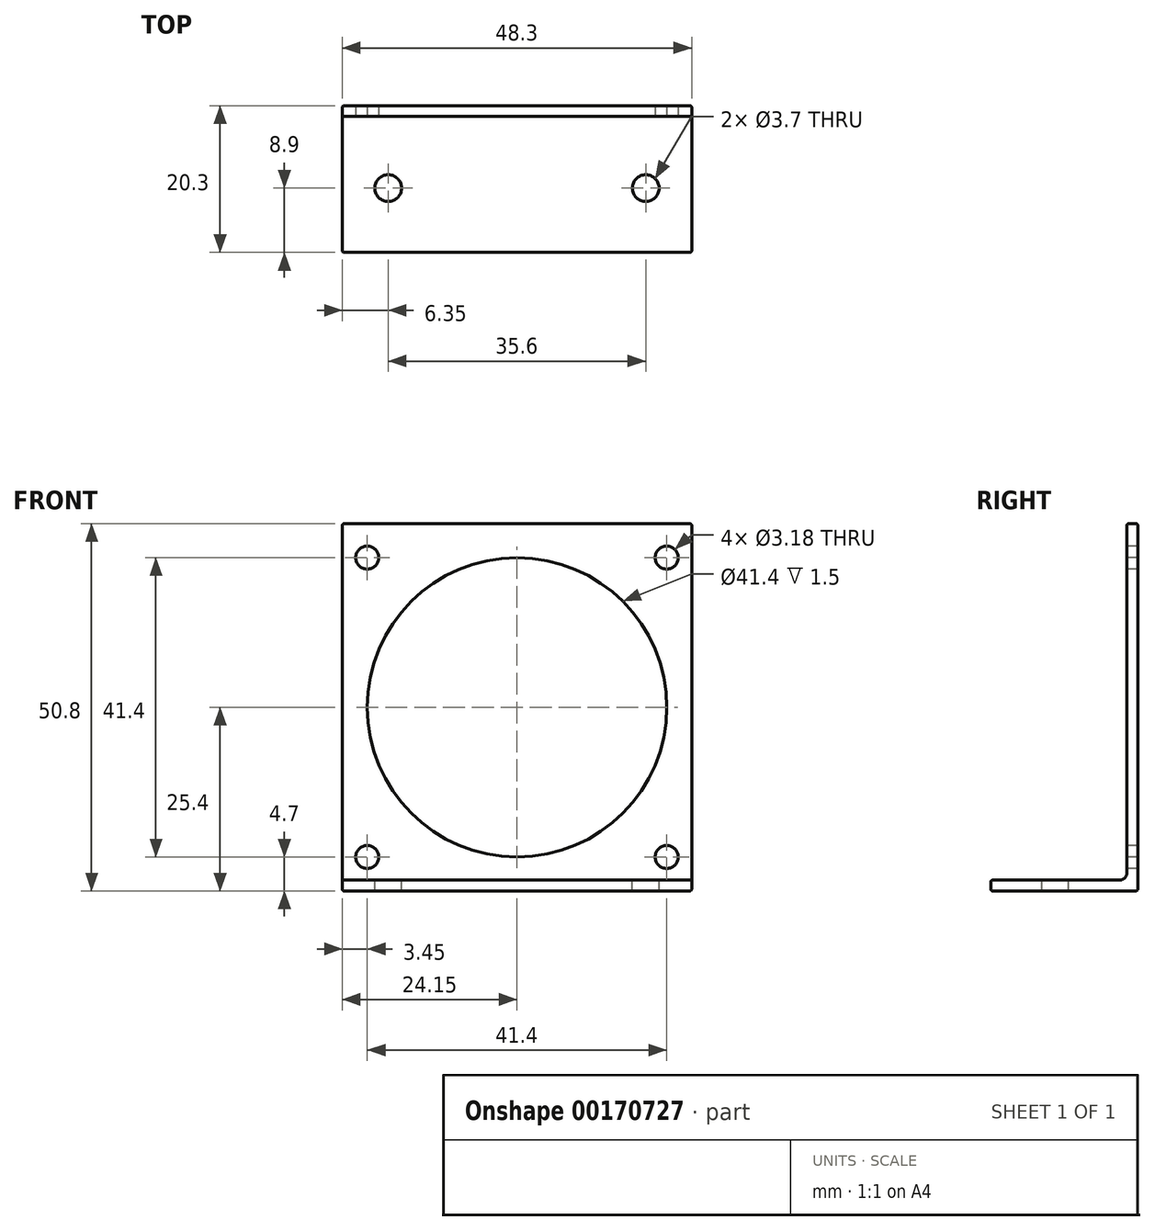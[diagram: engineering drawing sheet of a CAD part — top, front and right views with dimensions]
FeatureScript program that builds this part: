
annotation { "Feature Type Name" : "Feature", "Feature Type Description" : "" }
export const myFeature = defineFeature(function(context is Context, id is Id, definition is map)
    precondition{}
    {
        {
            var Q0;
            Q0=qCreatedBy(makeId("Right.planeOp"),FACE);
            var sketch = newSketch(context, id + "F0", { "sketchPlane" : qUnion([Q0])});
            skLineSegment(sketch, "E0.bottom", {"start": v(0.75, 25.4) * mm, "end": v(-0.75, 25.4) * mm});
            skLineSegment(sketch, "E0.top", {"start": v(0.75, -25.4) * mm, "end": v(-0.75, -25.4) * mm});
            skLineSegment(sketch, "E0.left", {"start": v(0.75, 25.4) * mm, "end": v(0.75, -25.4) * mm});
            skLineSegment(sketch, "E0.right", {"start": v(-0.75, 25.4) * mm, "end": v(-0.75, -25.4) * mm});
            skPoint(sketch, "E0.middle", {"position": v(0, 0) * mm});
            skLineSegment(sketch, "E1.bottom", {"start": v(-0.75, -25.4) * mm, "end": v(-19.55, -25.4) * mm});
            skLineSegment(sketch, "E1.top", {"start": v(-0.75, -23.9) * mm, "end": v(-19.55, -23.9) * mm});
            skLineSegment(sketch, "E1.left", {"start": v(-0.75, -25.4) * mm, "end": v(-0.75, -23.9) * mm});
            skLineSegment(sketch, "E1.right", {"start": v(-19.55, -25.4) * mm, "end": v(-19.55, -23.9) * mm});
            skSolve(sketch);
        }
        {
            var Q0;
            Q0=makeQuery(id+"F0.imprint","IMPRINT",FACE,{"disambiguationData":[TD([[makeQuery(id+"F0.imprint","IMPRINT",EDGE,{"derivedFrom":sQuery(id+"F0.wireOp",EDGE,"E1.bottom")}),-1.0]])]});
            var Q1;
            Q1=makeQuery(id+"F0.imprint","IMPRINT",FACE,{"disambiguationData":[TD([[makeQuery(id+"F0.imprint","IMPRINT",EDGE,{"derivedFrom":sQuery(id+"F0.wireOp",EDGE,"E0.bottom")}),1.0]])]});
            extrude(context, id + "F1", {"entities" : qUnion([Q0, Q1]), "depth" : 48.3 * mm});
        }
        {
            var Q0;
            Q0=makeQuery(id+"F1.opExtrude","SWEPT_EDGE",EDGE,{"disambiguationData":[OSD([sQuery(id+"F0.wireOp",EDGE,"E0.right"),sQuery(id+"F0.wireOp",EDGE,"E1.top"),sQuery(id+"F0.wireOp",EDGE,"E1.left")])]});
            fillet(context, id + "F2", {"entities" : qUnion([Q0]), "radius" : 1 * mm, "tangentPropagation" : true, "allowEdgeOverflow" : false});
        }
        {
            var Q0;
            Q0=makeQuery(id+"F1.opExtrude","SWEPT_FACE",FACE,{"disambiguationData":[OSD([sQuery(id+"F0.wireOp",EDGE,"E0.right")])]});
            var sketch = newSketch(context, id + "F3", { "sketchPlane" : qUnion([Q0])});
            skLineSegment(sketch, "E2.bottom", {"start": v(0, 25.4) * mm, "end": v(48.3, 25.4) * mm});
            skLineSegment(sketch, "E2.top", {"start": v(0, -23.9) * mm, "end": v(48.3, -23.9) * mm});
            skLineSegment(sketch, "E2.left", {"start": v(0, 25.4) * mm, "end": v(0, -23.9) * mm});
            skLineSegment(sketch, "E2.right", {"start": v(48.3, 25.4) * mm, "end": v(48.3, -23.9) * mm});
            skLineSegment(sketch, "E3", {"start": v(0, 0) * mm, "end": v(48.3, 0) * mm});
            skLineSegment(sketch, "E4.bottom", {"start": v(44.85, 20.7) * mm, "end": v(3.45, 20.7) * mm});
            skLineSegment(sketch, "E4.top", {"start": v(44.85, -20.7) * mm, "end": v(3.45, -20.7) * mm});
            skLineSegment(sketch, "E4.left", {"start": v(44.85, 20.7) * mm, "end": v(44.85, -20.7) * mm});
            skLineSegment(sketch, "E4.right", {"start": v(3.45, 20.7) * mm, "end": v(3.45, -20.7) * mm});
            skPoint(sketch, "E4.middle", {"position": v(24.15, 0) * mm});
            skSolve(sketch);
        }
        {
            var Q0;
            Q0=sQuery(id+"F3.wireOp",VERTEX,"E4.right.start");
            var Q1;
            Q1=sQuery(id+"F3.wireOp",VERTEX,"E4.left.start");
            var Q2;
            Q2=sQuery(id+"F3.wireOp",VERTEX,"E4.left.end");
            var Q3;
            Q3=sQuery(id+"F3.wireOp",VERTEX,"E4.right.end");
            var Q4;
            Q4=makeQuery(id+"F1.opExtrude","SWEPT_BODY",BODY,{"disambiguationData":[OSD([sQuery(id+"F0.wireOp",EDGE,"E0.bottom"),sQuery(id+"F0.wireOp",EDGE,"E0.top"),sQuery(id+"F0.wireOp",EDGE,"E0.left"),sQuery(id+"F0.wireOp",EDGE,"E0.right"),sQuery(id+"F0.wireOp",EDGE,"E1.bottom"),sQuery(id+"F0.wireOp",EDGE,"E1.top"),sQuery(id+"F0.wireOp",EDGE,"E1.right")])]});
            hole(context, id + "F4", {"style" : HoleStyle.SIMPLE, "endStyle" : HoleEndStyle.THROUGH, "holeDiameter" : 3.18 * mm, "locations" : qUnion([Q0, Q1, Q2, Q3]), "scope" : qUnion([Q4]), "isTappedThrough" : true});
        }
        {
            var Q0;
            Q0=makeQuery(id+"F1.opExtrude","SWEPT_FACE",FACE,{"disambiguationData":[OSD([sQuery(id+"F0.wireOp",EDGE,"E1.top")])]});
            var sketch = newSketch(context, id + "F5", { "sketchPlane" : qUnion([Q0])});
            skLineSegment(sketch, "E5.bottom", {"start": v(0, -1.75) * mm, "end": v(48.3, -1.75) * mm});
            skLineSegment(sketch, "E5.top", {"start": v(0, -19.55) * mm, "end": v(48.3, -19.55) * mm});
            skLineSegment(sketch, "E5.left", {"start": v(0, -1.75) * mm, "end": v(0, -19.55) * mm});
            skLineSegment(sketch, "E5.right", {"start": v(48.3, -1.75) * mm, "end": v(48.3, -19.55) * mm});
            skLineSegment(sketch, "E6", {"start": v(0, -10.65) * mm, "end": v(48.3, -10.65) * mm});
            skLineSegment(sketch, "E7.bottom", {"start": v(41.95, -1.25) * mm, "end": v(6.35, -1.25) * mm});
            skLineSegment(sketch, "E7.top", {"start": v(41.95, -20.05) * mm, "end": v(6.35, -20.05) * mm});
            skLineSegment(sketch, "E7.left", {"start": v(41.95, -1.25) * mm, "end": v(41.95, -20.05) * mm});
            skLineSegment(sketch, "E7.right", {"start": v(6.35, -1.25) * mm, "end": v(6.35, -20.05) * mm});
            skPoint(sketch, "E7.middle", {"position": v(24.15, -10.65) * mm});
            skPoint(sketch, "E8", {"position": v(6.35, -10.65) * mm});
            skPoint(sketch, "E9", {"position": v(41.95, -10.65) * mm});
            skSolve(sketch);
        }
        {
            var Q0;
            Q0=sQuery(id+"F5.wireOp",VERTEX,"E8");
            var Q1;
            Q1=sQuery(id+"F5.wireOp",VERTEX,"E9");
            var Q2;
            Q2=makeQuery(id+"F1.opExtrude","SWEPT_BODY",BODY,{"disambiguationData":[OSD([sQuery(id+"F0.wireOp",EDGE,"E0.bottom"),sQuery(id+"F0.wireOp",EDGE,"E0.top"),sQuery(id+"F0.wireOp",EDGE,"E0.left"),sQuery(id+"F0.wireOp",EDGE,"E0.right"),sQuery(id+"F0.wireOp",EDGE,"E1.bottom"),sQuery(id+"F0.wireOp",EDGE,"E1.top"),sQuery(id+"F0.wireOp",EDGE,"E1.right")])]});
            hole(context, id + "F6", {"style" : HoleStyle.SIMPLE, "endStyle" : HoleEndStyle.THROUGH, "holeDiameter" : 3.7 * mm, "locations" : qUnion([Q0, Q1]), "scope" : qUnion([Q2]), "isTappedThrough" : true});
        }
        {
            var Q0;
            Q0=sQuery(id+"F3.wireOp",VERTEX,"E4.middle");
            var Q1;
            Q1=makeQuery(id+"F1.opExtrude","SWEPT_BODY",BODY,{"disambiguationData":[OSD([sQuery(id+"F0.wireOp",EDGE,"E0.bottom"),sQuery(id+"F0.wireOp",EDGE,"E0.top"),sQuery(id+"F0.wireOp",EDGE,"E0.left"),sQuery(id+"F0.wireOp",EDGE,"E0.right"),sQuery(id+"F0.wireOp",EDGE,"E1.bottom"),sQuery(id+"F0.wireOp",EDGE,"E1.top"),sQuery(id+"F0.wireOp",EDGE,"E1.right")])]});
            hole(context, id + "F7", {"style" : HoleStyle.SIMPLE, "endStyle" : HoleEndStyle.THROUGH, "holeDiameter" : 41.4 * mm, "locations" : qUnion([Q0]), "scope" : qUnion([Q1]), "isTappedThrough" : true});
        }
        {
            var Q0;
            Q0=makeQuery(id+"F7.hole-0.boolean.opBoolean","COPY",EDGE,{"derivedFrom":makeQuery(id+"F7.hole-0.opRevolve","SWEPT_EDGE",EDGE,{"disambiguationData":[OSD([sQuery(id+"F7.hole-0.sketch.wireOp",EDGE,"core_line_2"),sQuery(id+"F7.hole-0.sketch.wireOp",EDGE,"core_line_3")])]})});
            var Q1;
            Q1=makeQuery(id+"F7.hole-0.boolean.opBoolean","INTERSECT",EDGE,{"derivedFrom":[makeQuery(id+"F1.opExtrude","SWEPT_FACE",FACE,{"disambiguationData":[OSD([sQuery(id+"F0.wireOp",EDGE,"E0.left")])]}),makeQuery(id+"F7.hole-0.opRevolve","SWEPT_FACE",FACE,{"disambiguationData":[OSD([sQuery(id+"F7.hole-0.sketch.wireOp",EDGE,"core_line_2")])]})]});
            var Q2;
            Q2=makeQuery(id+"F4.hole-0.boolean.opBoolean","COPY",EDGE,{"derivedFrom":makeQuery(id+"F4.hole-0.opRevolve","SWEPT_EDGE",EDGE,{"disambiguationData":[OSD([sQuery(id+"F4.hole-0.sketch.wireOp",EDGE,"core_line_2"),sQuery(id+"F4.hole-0.sketch.wireOp",EDGE,"core_line_3")])]})});
            var Q3;
            Q3=makeQuery(id+"F4.hole-1.boolean.opBoolean","COPY",EDGE,{"derivedFrom":makeQuery(id+"F4.hole-1.opRevolve","SWEPT_EDGE",EDGE,{"disambiguationData":[OSD([sQuery(id+"F4.hole-1.sketch.wireOp",EDGE,"core_line_2"),sQuery(id+"F4.hole-1.sketch.wireOp",EDGE,"core_line_3")])]})});
            var Q4;
            Q4=makeQuery(id+"F4.hole-3.boolean.opBoolean","COPY",EDGE,{"derivedFrom":makeQuery(id+"F4.hole-3.opRevolve","SWEPT_EDGE",EDGE,{"disambiguationData":[OSD([sQuery(id+"F4.hole-3.sketch.wireOp",EDGE,"core_line_2"),sQuery(id+"F4.hole-3.sketch.wireOp",EDGE,"core_line_3")])]})});
            var Q5;
            Q5=makeQuery(id+"F4.hole-2.boolean.opBoolean","COPY",EDGE,{"derivedFrom":makeQuery(id+"F4.hole-2.opRevolve","SWEPT_EDGE",EDGE,{"disambiguationData":[OSD([sQuery(id+"F4.hole-2.sketch.wireOp",EDGE,"core_line_2"),sQuery(id+"F4.hole-2.sketch.wireOp",EDGE,"core_line_3")])]})});
            var Q6;
            Q6=makeQuery(id+"F6.hole-1.boolean.opBoolean","COPY",EDGE,{"derivedFrom":makeQuery(id+"F6.hole-1.opRevolve","SWEPT_EDGE",EDGE,{"disambiguationData":[OSD([sQuery(id+"F6.hole-1.sketch.wireOp",EDGE,"core_line_2"),sQuery(id+"F6.hole-1.sketch.wireOp",EDGE,"core_line_3")])]})});
            var Q7;
            Q7=makeQuery(id+"F6.hole-0.boolean.opBoolean","COPY",EDGE,{"derivedFrom":makeQuery(id+"F6.hole-0.opRevolve","SWEPT_EDGE",EDGE,{"disambiguationData":[OSD([sQuery(id+"F6.hole-0.sketch.wireOp",EDGE,"core_line_2"),sQuery(id+"F6.hole-0.sketch.wireOp",EDGE,"core_line_3")])]})});
            var Q8;
            Q8=makeQuery(id+"F6.hole-1.boolean.opBoolean","INTERSECT",EDGE,{"derivedFrom":[makeQuery(id+"F1.opExtrude","SWEPT_FACE",FACE,{"disambiguationData":[OSD([sQuery(id+"F0.wireOp",EDGE,"E0.top"),sQuery(id+"F0.wireOp",EDGE,"E1.bottom")])]}),makeQuery(id+"F6.hole-1.opRevolve","SWEPT_FACE",FACE,{"disambiguationData":[OSD([sQuery(id+"F6.hole-1.sketch.wireOp",EDGE,"core_line_2")])]})]});
            var Q9;
            Q9=makeQuery(id+"F6.hole-0.boolean.opBoolean","INTERSECT",EDGE,{"derivedFrom":[makeQuery(id+"F1.opExtrude","SWEPT_FACE",FACE,{"disambiguationData":[OSD([sQuery(id+"F0.wireOp",EDGE,"E0.top"),sQuery(id+"F0.wireOp",EDGE,"E1.bottom")])]}),makeQuery(id+"F6.hole-0.opRevolve","SWEPT_FACE",FACE,{"disambiguationData":[OSD([sQuery(id+"F6.hole-0.sketch.wireOp",EDGE,"core_line_2")])]})]});
            var Q10;
            Q10=makeQuery(id+"F4.hole-3.boolean.opBoolean","INTERSECT",EDGE,{"derivedFrom":[makeQuery(id+"F1.opExtrude","SWEPT_FACE",FACE,{"disambiguationData":[OSD([sQuery(id+"F0.wireOp",EDGE,"E0.left")])]}),makeQuery(id+"F4.hole-3.opRevolve","SWEPT_FACE",FACE,{"disambiguationData":[OSD([sQuery(id+"F4.hole-3.sketch.wireOp",EDGE,"core_line_2")])]})]});
            var Q11;
            Q11=makeQuery(id+"F4.hole-2.boolean.opBoolean","INTERSECT",EDGE,{"derivedFrom":[makeQuery(id+"F1.opExtrude","SWEPT_FACE",FACE,{"disambiguationData":[OSD([sQuery(id+"F0.wireOp",EDGE,"E0.left")])]}),makeQuery(id+"F4.hole-2.opRevolve","SWEPT_FACE",FACE,{"disambiguationData":[OSD([sQuery(id+"F4.hole-2.sketch.wireOp",EDGE,"core_line_2")])]})]});
            var Q12;
            Q12=makeQuery(id+"F4.hole-1.boolean.opBoolean","INTERSECT",EDGE,{"derivedFrom":[makeQuery(id+"F1.opExtrude","SWEPT_FACE",FACE,{"disambiguationData":[OSD([sQuery(id+"F0.wireOp",EDGE,"E0.left")])]}),makeQuery(id+"F4.hole-1.opRevolve","SWEPT_FACE",FACE,{"disambiguationData":[OSD([sQuery(id+"F4.hole-1.sketch.wireOp",EDGE,"core_line_2")])]})]});
            var Q13;
            Q13=makeQuery(id+"F4.hole-0.boolean.opBoolean","INTERSECT",EDGE,{"derivedFrom":[makeQuery(id+"F1.opExtrude","SWEPT_FACE",FACE,{"disambiguationData":[OSD([sQuery(id+"F0.wireOp",EDGE,"E0.left")])]}),makeQuery(id+"F4.hole-0.opRevolve","SWEPT_FACE",FACE,{"disambiguationData":[OSD([sQuery(id+"F4.hole-0.sketch.wireOp",EDGE,"core_line_2")])]})]});
            var Q14;
            Q14=makeQuery(id+"F1.opExtrude","SWEPT_EDGE",EDGE,{"disambiguationData":[OSD([sQuery(id+"F0.wireOp",EDGE,"E0.bottom"),sQuery(id+"F0.wireOp",EDGE,"E0.left")])]});
            var Q15;
            Q15=makeQuery(id+"F1.opExtrude","CAP_EDGE",EDGE,{"disambiguationData":[OSD([sQuery(id+"F0.wireOp",EDGE,"E0.left")])],"isStart":true});
            var Q16;
            Q16=makeQuery(id+"F1.opExtrude","SWEPT_EDGE",EDGE,{"disambiguationData":[OSD([sQuery(id+"F0.wireOp",EDGE,"E0.top"),sQuery(id+"F0.wireOp",EDGE,"E0.left")])]});
            var Q17;
            Q17=makeQuery(id+"F1.opExtrude","CAP_EDGE",EDGE,{"disambiguationData":[OSD([sQuery(id+"F0.wireOp",EDGE,"E0.left")])],"isStart":false});
            var Q18;
            Q18=makeQuery(id+"F1.opExtrude","CAP_EDGE",EDGE,{"disambiguationData":[OSD([sQuery(id+"F0.wireOp",EDGE,"E0.bottom")])],"isStart":true});
            var Q19;
            Q19=makeQuery(id+"F1.opExtrude","CAP_EDGE",EDGE,{"disambiguationData":[OSD([sQuery(id+"F0.wireOp",EDGE,"E0.bottom")])],"isStart":false});
            var Q20;
            Q20=makeQuery(id+"F1.opExtrude","SWEPT_EDGE",EDGE,{"disambiguationData":[OSD([sQuery(id+"F0.wireOp",EDGE,"E0.bottom"),sQuery(id+"F0.wireOp",EDGE,"E0.right")])]});
            var Q21;
            Q21=makeQuery(id+"F1.opExtrude","CAP_EDGE",EDGE,{"disambiguationData":[OSD([sQuery(id+"F0.wireOp",EDGE,"E0.right")])],"isStart":false});
            var Q22;
            Q22=makeQuery(id+"F1.opExtrude","CAP_EDGE",EDGE,{"disambiguationData":[OSD([sQuery(id+"F0.wireOp",EDGE,"E0.right")])],"isStart":true});
            var Q23;
            Q23=makeQuery(id+"F1.opExtrude","CAP_EDGE",EDGE,{"disambiguationData":[OSD([sQuery(id+"F0.wireOp",EDGE,"E1.top")])],"isStart":true});
            var Q24;
            {var subQ0=sQuery(id+"F0.wireOp",EDGE,"E1.top");var subQ1=sQuery(id+"F0.wireOp",EDGE,"E0.right");Q24=makeQuery(id+"F2.opFillet","BLEND_EDGE",EDGE,{"blendedFrom":[makeQuery(id+"F1.opExtrude","SWEPT_EDGE",EDGE,{"disambiguationData":[OSD([subQ1,subQ0,sQuery(id+"F0.wireOp",EDGE,"E1.left")])]}),makeQuery(id+"F1.opExtrude","CAP_FACE",FACE,{"disambiguationData":[OSD([sQuery(id+"F0.wireOp",EDGE,"E0.bottom"),sQuery(id+"F0.wireOp",EDGE,"E0.top"),sQuery(id+"F0.wireOp",EDGE,"E0.left"),subQ1,sQuery(id+"F0.wireOp",EDGE,"E1.bottom"),subQ0,sQuery(id+"F0.wireOp",EDGE,"E1.right")])],"isStart":true})],"blendedInto":[makeQuery(id+"F1.opExtrude","CAP_FACE",FACE,{"disambiguationData":[OSD([sQuery(id+"F0.wireOp",EDGE,"E0.bottom"),sQuery(id+"F0.wireOp",EDGE,"E0.top"),sQuery(id+"F0.wireOp",EDGE,"E0.left"),subQ1,sQuery(id+"F0.wireOp",EDGE,"E1.bottom"),subQ0,sQuery(id+"F0.wireOp",EDGE,"E1.right")])],"isStart":true})]});}
            var Q25;
            Q25=makeQuery(id+"F1.opExtrude","CAP_EDGE",EDGE,{"disambiguationData":[OSD([sQuery(id+"F0.wireOp",EDGE,"E1.top")])],"isStart":false});
            var Q26;
            {var subQ0=sQuery(id+"F0.wireOp",EDGE,"E1.top");var subQ1=sQuery(id+"F0.wireOp",EDGE,"E0.right");Q26=makeQuery(id+"F2.opFillet","BLEND_EDGE",EDGE,{"blendedFrom":[makeQuery(id+"F1.opExtrude","SWEPT_EDGE",EDGE,{"disambiguationData":[OSD([subQ1,subQ0,sQuery(id+"F0.wireOp",EDGE,"E1.left")])]}),makeQuery(id+"F1.opExtrude","CAP_FACE",FACE,{"disambiguationData":[OSD([sQuery(id+"F0.wireOp",EDGE,"E0.bottom"),sQuery(id+"F0.wireOp",EDGE,"E0.top"),sQuery(id+"F0.wireOp",EDGE,"E0.left"),subQ1,sQuery(id+"F0.wireOp",EDGE,"E1.bottom"),subQ0,sQuery(id+"F0.wireOp",EDGE,"E1.right")])],"isStart":false})],"blendedInto":[makeQuery(id+"F1.opExtrude","CAP_FACE",FACE,{"disambiguationData":[OSD([sQuery(id+"F0.wireOp",EDGE,"E0.bottom"),sQuery(id+"F0.wireOp",EDGE,"E0.top"),sQuery(id+"F0.wireOp",EDGE,"E0.left"),subQ1,sQuery(id+"F0.wireOp",EDGE,"E1.bottom"),subQ0,sQuery(id+"F0.wireOp",EDGE,"E1.right")])],"isStart":false})]});}
            var Q27;
            Q27=makeQuery(id+"F1.opExtrude","CAP_EDGE",EDGE,{"disambiguationData":[OSD([sQuery(id+"F0.wireOp",EDGE,"E0.top"),sQuery(id+"F0.wireOp",EDGE,"E1.bottom")])],"isStart":true});
            var Q28;
            Q28=makeQuery(id+"F1.opExtrude","SWEPT_EDGE",EDGE,{"disambiguationData":[OSD([sQuery(id+"F0.wireOp",EDGE,"E1.bottom"),sQuery(id+"F0.wireOp",EDGE,"E1.right")])]});
            var Q29;
            Q29=makeQuery(id+"F1.opExtrude","CAP_EDGE",EDGE,{"disambiguationData":[OSD([sQuery(id+"F0.wireOp",EDGE,"E1.right")])],"isStart":true});
            var Q30;
            Q30=makeQuery(id+"F1.opExtrude","CAP_EDGE",EDGE,{"disambiguationData":[OSD([sQuery(id+"F0.wireOp",EDGE,"E0.top"),sQuery(id+"F0.wireOp",EDGE,"E1.bottom")])],"isStart":false});
            var Q31;
            Q31=makeQuery(id+"F1.opExtrude","SWEPT_EDGE",EDGE,{"disambiguationData":[OSD([sQuery(id+"F0.wireOp",EDGE,"E1.top"),sQuery(id+"F0.wireOp",EDGE,"E1.right")])]});
            var Q32;
            Q32=makeQuery(id+"F1.opExtrude","CAP_EDGE",EDGE,{"disambiguationData":[OSD([sQuery(id+"F0.wireOp",EDGE,"E1.right")])],"isStart":false});
            fillet(context, id + "F8", {"entities" : qUnion([Q0, Q1, Q2, Q3, Q4, Q5, Q6, Q7, Q8, Q9, Q10, Q11, Q12, Q13, Q14, Q15, Q16, Q17, Q18, Q19, Q20, Q21, Q22, Q23, Q24, Q25, Q26, Q27, Q28, Q29, Q30, Q31, Q32]), "radius" : 0.25 * mm, "tangentPropagation" : true, "allowEdgeOverflow" : false});
        }
    });
